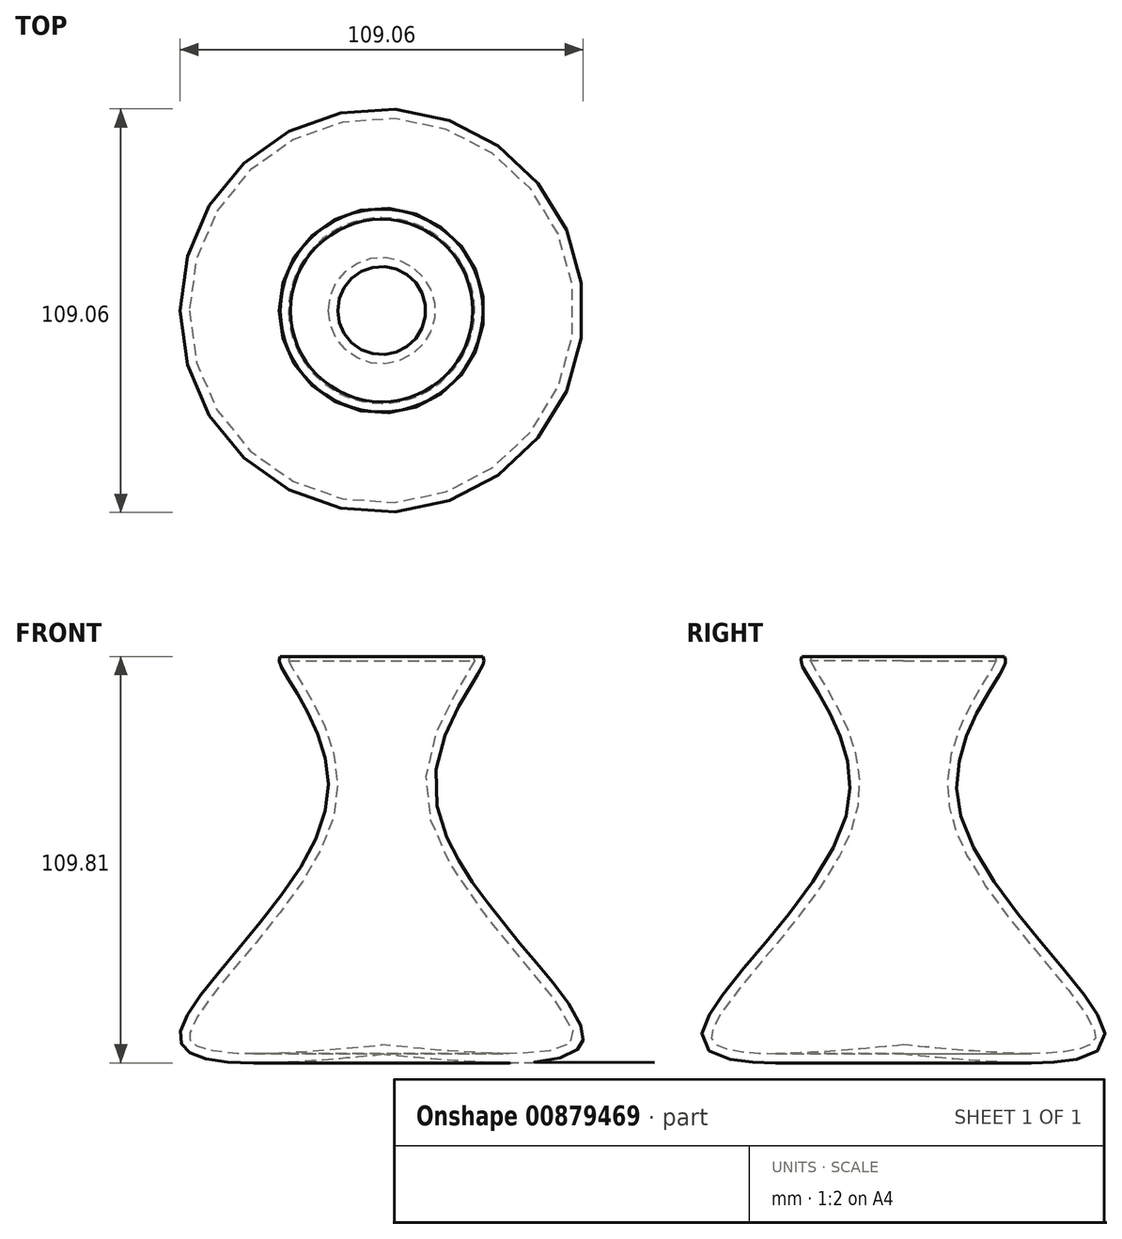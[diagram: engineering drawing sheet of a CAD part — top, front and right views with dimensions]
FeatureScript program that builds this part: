
annotation { "Feature Type Name" : "Feature", "Feature Type Description" : "" }
export const myFeature = defineFeature(function(context is Context, id is Id, definition is map)
    precondition{}
    {
        {
            var Q0;
            Q0=qCreatedBy(makeId("Front.planeOp"),FACE);
            var sketch = newSketch(context, id + "F0", { "sketchPlane" : qUnion([Q0])});
            skLineSegment(sketch, "E0", {"start": v(0, 59.44) * mm, "end": v(0, -48.07) * mm});
            skLineSegment(sketch, "E1", {"start": v(0, 59.44) * mm, "end": v(-27.4, 59.44) * mm});
            skFitSpline(sketch, "E2", {"points": [v(-27.4, 59.44) * mm, v(-27.4, 57.17) * mm, v(-14.89, 19.24) * mm, v(-54.52, -43.5) * mm, v(0, -48.07) * mm], "startDerivative": vector(-10.7, -26.34) * mm, "endDerivative": vector(261.74, 24.41) * mm});
            skSolve(sketch);
        }
        {
            var Q0;
            Q0=makeQuery(id+"F0.imprint","IMPRINT",FACE,{"disambiguationData":[TD([[makeQuery(id+"F0.imprint","IMPRINT",EDGE,{"derivedFrom":sQuery(id+"F0.wireOp",EDGE,"E0")}),-1.0]])]});
            var Q1;
            Q1=sQuery(id+"F0.wireOp",EDGE,"E0");
            revolve(context, id + "F1", {"surfaceOperationType" : NewSurfaceOperationType.NEW, "entities" : qUnion([Q0]), "axis" : qUnion([Q1]), "revolveType" : RevolveType.FULL});
        }
        {
            var Q0;
            Q0=makeQuery(id+"F1.opRevolve","SWEPT_FACE",FACE,{"disambiguationData":[OSD([sQuery(id+"F0.wireOp",EDGE,"E1")])]});
            shell(context, id + "F2", {"entities" : qUnion([Q0]), "thickness" : 2.54 * mm});
        }
    });
